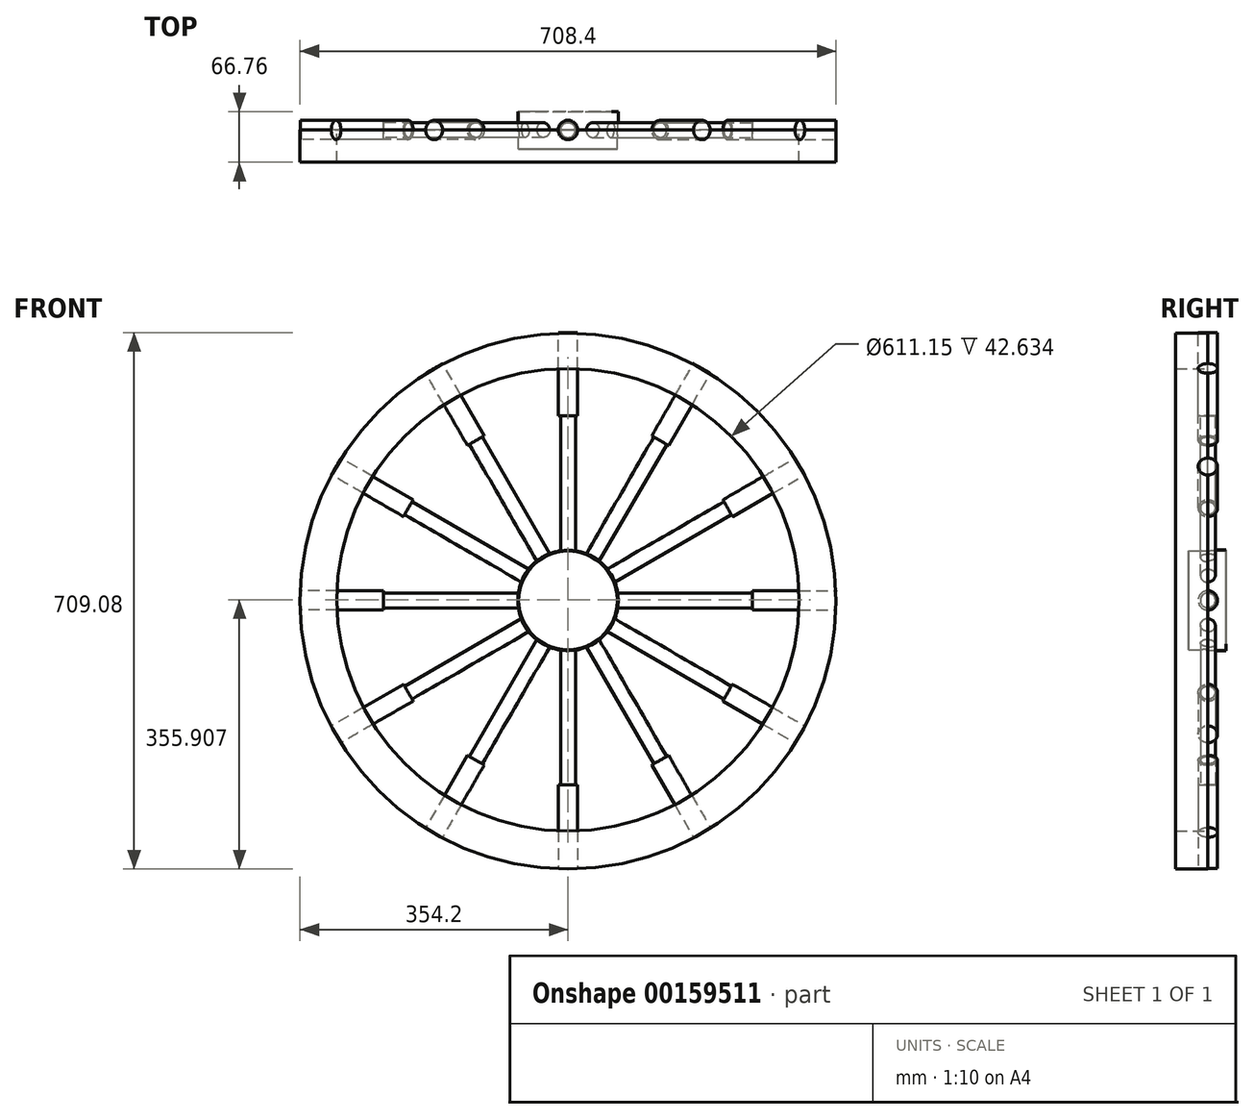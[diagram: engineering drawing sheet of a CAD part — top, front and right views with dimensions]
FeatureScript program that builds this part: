
annotation { "Feature Type Name" : "Feature", "Feature Type Description" : "" }
export const myFeature = defineFeature(function(context is Context, id is Id, definition is map)
    precondition{}
    {
        {
            var Q0;
            Q0=qCreatedBy(makeId("Top.planeOp"),FACE);
            var sketch = newSketch(context, id + "F0", { "sketchPlane" : qUnion([Q0])});
            skCircle(sketch, "E0", {"center": v(0, 0) * mm, "radius": 12.81 * mm});
            skSolve(sketch);
        }
        {
            var Q0;
            Q0=makeQuery(id+"F0.imprint","IMPRINT",FACE,{"disambiguationData":[TD([[makeQuery(id+"F0.imprint","IMPRINT",EDGE,{"derivedFrom":sQuery(id+"F0.wireOp",EDGE,"E0")}),1.0]])]});
            extrude(context, id + "F1", {"entities" : qUnion([Q0]), "depth" : 110.23 * mm});
        }
        {
            var Q0;
            Q0=makeQuery(id+"F1.opExtrude","CAP_FACE",FACE,{"disambiguationData":[OSD([sQuery(id+"F0.wireOp",EDGE,"E0")])],"isStart":false});
            var sketch = newSketch(context, id + "F2", { "sketchPlane" : qUnion([Q0])});
            skCircle(sketch, "E1", {"center": v(0, 0) * mm, "radius": 9.86 * mm});
            skSolve(sketch);
        }
        {
            var Q0;
            Q0=makeQuery(id+"F2.imprint","IMPRINT",FACE,{"disambiguationData":[TD([[makeQuery(id+"F2.imprint","IMPRINT",EDGE,{"derivedFrom":sQuery(id+"F2.wireOp",EDGE,"E1")}),1.0]])]});
            extrude(context, id + "F3", {"entities" : qUnion([Q0]), "operationType" : NewBodyOperationType.ADD, "depth" : 210.1 * mm});
        }
        {
            var Q0;
            Q0=qCreatedBy(makeId("Front.planeOp"),FACE);
            var sketch = newSketch(context, id + "F4", { "sketchPlane" : qUnion([Q0])});
            skCircle(sketch, "E2", {"center": v(0, 353.97) * mm, "radius": 65.41 * mm});
            skSolve(sketch);
        }
        {
            var Q0;
            Q0=makeQuery(id+"F4.imprint","IMPRINT",FACE,{"disambiguationData":[TD([[makeQuery(id+"F4.imprint","IMPRINT",EDGE,{"derivedFrom":sQuery(id+"F4.wireOp",EDGE,"E2")}),1.0]])]});
            extrude(context, id + "F5", {"entities" : qUnion([Q0]), "operationType" : NewBodyOperationType.ADD, "depth" : 25.4 * mm});
        }
        {
            var Q0;
            Q0=qCreatedBy(makeId("Front.planeOp"),FACE);
            var sketch = newSketch(context, id + "F6", { "sketchPlane" : qUnion([Q0])});
            skCircle(sketch, "E3", {"center": v(0, 353.25) * mm, "radius": 65.73 * mm});
            skSolve(sketch);
        }
        {
            var Q0;
            Q0 = qSketchRegion(id + "F6", true);
            extrude(context, id + "F7", {"entities" : qUnion([Q0]), "operationType" : NewBodyOperationType.ADD, "oppositeDirection" : true, "depth" : 24.13 * mm});
        }
        {
            var Q0;
            Q0=makeQuery(id+"F1.opExtrude","SWEPT_BODY",BODY,{"disambiguationData":[OSD([sQuery(id+"F0.wireOp",EDGE,"E0")])]});
            var Q1;
            Q1=makeQuery(id+"F5.opExtrude","SWEPT_FACE",FACE,{"disambiguationData":[OSD([sQuery(id+"F4.wireOp",EDGE,"E2")])]});
            circularPattern(context, id + "F8", {"entities" : qUnion([Q0]), "axis" : qUnion([Q1]), "angle" : 30 * degree, "instanceCount" : 14});
        }
        {
            var Q0;
            Q0=qCreatedBy(makeId("Front.planeOp"),FACE);
            var sketch = newSketch(context, id + "F9", { "sketchPlane" : qUnion([Q0])});
            skCircle(sketch, "E4", {"center": v(0, 353.06) * mm, "radius": 354.2 * mm});
            skSolve(sketch);
        }
        {
            var Q0;
            Q0=makeQuery(id+"F9.imprint","IMPRINT",FACE,{"disambiguationData":[TD([[makeQuery(id+"F9.imprint","IMPRINT",EDGE,{"derivedFrom":sQuery(id+"F9.wireOp",EDGE,"E4")}),1.0]])]});
            var sketch = newSketch(context, id + "F10", { "sketchPlane" : qUnion([Q0])});
            skCircle(sketch, "E5", {"center": v(0, 354.76) * mm, "radius": 305.57 * mm});
            skSolve(sketch);
        }
        {
            var Q0;
            Q0=makeQuery(id+"F10.imprint","IMPRINT",FACE,{"disambiguationData":[TD([[makeQuery(id+"F10.imprint","IMPRINT",EDGE,{"derivedFrom":sQuery(id+"F10.wireOp",EDGE,"E5")}),-1.0]])]});
            extrude(context, id + "F11", {"entities" : qUnion([Q0]), "depth" : 42.63 * mm});
        }
    });
